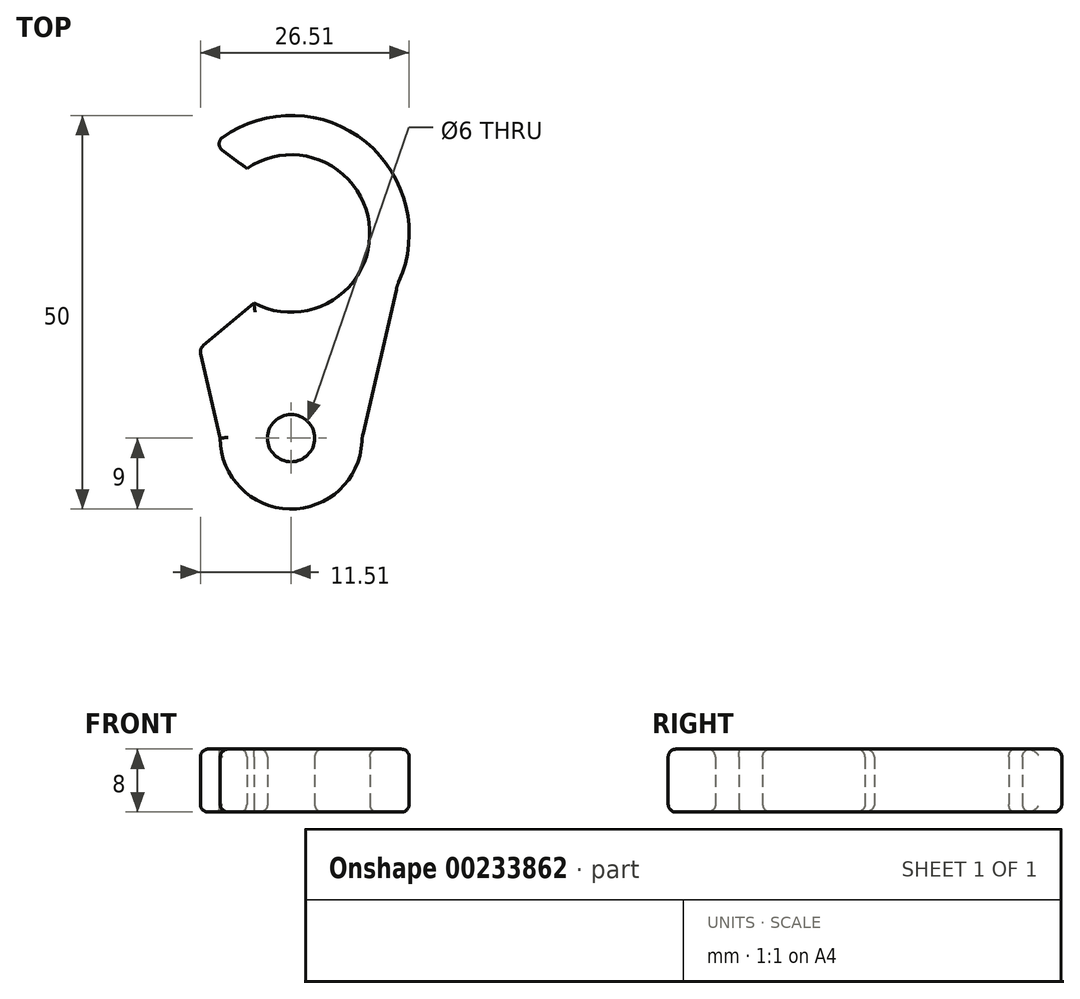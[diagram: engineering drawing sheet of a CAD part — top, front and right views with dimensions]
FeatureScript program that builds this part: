
annotation { "Feature Type Name" : "Feature", "Feature Type Description" : "" }
export const myFeature = defineFeature(function(context is Context, id is Id, definition is map)
    precondition{}
    {
        {
            var Q0;
            Q0=qCreatedBy(makeId("Top.planeOp"),FACE);
            var sketch = newSketch(context, id + "F0", { "sketchPlane" : qUnion([Q0])});
            skCircle(sketch, "E0", {"center": v(0, 0) * mm, "radius": 10 * mm});
            skCircle(sketch, "E1", {"center": v(0, 0) * mm, "radius": 15 * mm});
            skLineSegment(sketch, "E2", {"start": v(0, 0) * mm, "end": v(0, -26) * mm});
            skCircle(sketch, "E3", {"center": v(0, -26) * mm, "radius": 3 * mm});
            skCircle(sketch, "E4", {"center": v(0, -26) * mm, "radius": 9 * mm});
            skLineSegment(sketch, "E5", {"start": v(0, 0) * mm, "end": v(-15, 0) * mm});
            skLineSegment(sketch, "E6", {"start": v(-15, 0) * mm, "end": v(-9, -26) * mm});
            skLineSegment(sketch, "E7", {"start": v(0, 0) * mm, "end": v(15, 0) * mm});
            skLineSegment(sketch, "E8", {"start": v(15, 0) * mm, "end": v(9, -26) * mm});
            skLineSegment(sketch, "E9", {"start": v(-9.8, 11.36) * mm, "end": v(-5.61, 8.28) * mm});
            skLineSegment(sketch, "E10", {"start": v(-4.72, -8.81) * mm, "end": v(-11.62, -14.65) * mm});
            skSolve(sketch);
        }
        {
            var Q0;
            {var subQ0=sQuery(id+"F0.wireOp",EDGE,"E9");Q0=makeQuery(id+"F0.imprint","IMPRINT",FACE,{"disambiguationData":[TD([[makeQuery(id+"F0.imprint","IMPRINT",EDGE,{"derivedFrom":subQ0}),1.0]])]});}
            var Q1;
            {var subQ1=sQuery(id+"F0.wireOp",EDGE,"E0");var subQ6=sQuery(id+"F0.wireOp",EDGE,"E7");var subQ8=makeQuery(id+"F0.imprint","INTERSECT",VERTEX,{"derivedFrom":[subQ1,subQ6]});Q1=makeQuery(id+"F0.imprint","IMPRINT",FACE,{"disambiguationData":[TD([[makeQuery(id+"F0.imprint","IMPRINT",EDGE,{"disambiguationData":[TD([[subQ8,1.0]])],"derivedFrom":subQ1}),-1.0]])]});}
            var Q2;
            {var subQ0=sQuery(id+"F0.wireOp",EDGE,"E8");var subQ1=sQuery(id+"F0.wireOp",EDGE,"E1");var subQ2=makeQuery(id+"F0.imprint","INTERSECT",VERTEX,{"derivedFrom":[subQ1,subQ0]});Q2=makeQuery(id+"F0.imprint","IMPRINT",FACE,{"disambiguationData":[TD([[makeQuery(id+"F0.imprint","IMPRINT",EDGE,{"disambiguationData":[TD([[subQ2,1.0]])],"derivedFrom":subQ1}),-1.0]])]});}
            var Q3;
            Q3=makeQuery(id+"F0.imprint","IMPRINT",FACE,{"disambiguationData":[TD([[makeQuery(id+"F0.imprint","IMPRINT",EDGE,{"derivedFrom":sQuery(id+"F0.wireOp",EDGE,"E3")}),-1.0]])]});
            var Q4;
            {var subQ3=sQuery(id+"F0.wireOp",EDGE,"E10");var subQ5=sQuery(id+"F0.wireOp",EDGE,"E1");var subQ6=makeQuery(id+"F0.imprint","INTERSECT",VERTEX,{"derivedFrom":[subQ5,subQ3]});Q4=makeQuery(id+"F0.imprint","IMPRINT",FACE,{"disambiguationData":[TD([[makeQuery(id+"F0.imprint","IMPRINT",EDGE,{"disambiguationData":[TD([[subQ6,-1.0]])],"derivedFrom":subQ5}),-1.0]])]});}
            var Q5;
            {var subQ0=sQuery(id+"F0.wireOp",EDGE,"E10");var subQ1=sQuery(id+"F0.wireOp",EDGE,"E0");var subQ2=makeQuery(id+"F0.imprint","INTERSECT",VERTEX,{"derivedFrom":[subQ1,subQ0]});Q5=makeQuery(id+"F0.imprint","IMPRINT",FACE,{"disambiguationData":[TD([[makeQuery(id+"F0.imprint","IMPRINT",EDGE,{"disambiguationData":[TD([[subQ2,-1.0]])],"derivedFrom":subQ1}),-1.0]])]});}
            var Q6;
            {var subQ0=sQuery(id+"F0.wireOp",EDGE,"E8");var subQ1=sQuery(id+"F0.wireOp",EDGE,"E1");var subQ3=makeQuery(id+"F0.imprint","INTERSECT",VERTEX,{"derivedFrom":[subQ1,subQ0]});Q6=makeQuery(id+"F0.imprint","IMPRINT",FACE,{"disambiguationData":[TD([[makeQuery(id+"F0.imprint","IMPRINT",EDGE,{"disambiguationData":[TD([[subQ3,-1.0]])],"derivedFrom":subQ1}),1.0]])]});}
            extrude(context, id + "F1", {"entities" : qUnion([Q0, Q1, Q2, Q3, Q4, Q5, Q6]), "depth" : 8 * mm});
        }
        {
            var Q0;
            Q0=makeQuery(id+"F1.opExtrude","SWEPT_EDGE",EDGE,{"disambiguationData":[OSD([sQuery(id+"F0.wireOp",EDGE,"E1"),sQuery(id+"F0.wireOp",EDGE,"E8")])]});
            var Q1;
            Q1=makeQuery(id+"F1.opExtrude","SWEPT_EDGE",EDGE,{"disambiguationData":[OSD([sQuery(id+"F0.wireOp",EDGE,"E4"),sQuery(id+"F0.wireOp",EDGE,"E8")])]});
            fillet(context, id + "F2", {"entities" : qUnion([Q0, Q1]), "radius" : 5 * mm, "tangentPropagation" : true, "allowEdgeOverflow" : false});
        }
        {
            var Q0;
            Q0=makeQuery(id+"F1.opExtrude","CAP_EDGE",EDGE,{"disambiguationData":[OSD([sQuery(id+"F0.wireOp",EDGE,"E3")])],"isStart":true});
            var Q1;
            Q1=makeQuery(id+"F1.opExtrude","CAP_EDGE",EDGE,{"disambiguationData":[OSD([sQuery(id+"F0.wireOp",EDGE,"E3")])],"isStart":false});
            var Q2;
            Q2=makeQuery(id+"F1.opExtrude","CAP_EDGE",EDGE,{"disambiguationData":[OSD([sQuery(id+"F0.wireOp",EDGE,"E0")])],"isStart":false});
            var Q3;
            Q3=makeQuery(id+"F1.opExtrude","CAP_EDGE",EDGE,{"disambiguationData":[OSD([sQuery(id+"F0.wireOp",EDGE,"E0")])],"isStart":true});
            var Q4;
            Q4=makeQuery(id+"F1.opExtrude","CAP_EDGE",EDGE,{"disambiguationData":[OSD([sQuery(id+"F0.wireOp",EDGE,"E10")])],"isStart":false});
            var Q5;
            Q5=makeQuery(id+"F1.opExtrude","CAP_EDGE",EDGE,{"disambiguationData":[OSD([sQuery(id+"F0.wireOp",EDGE,"E10")])],"isStart":true});
            var Q6;
            Q6=makeQuery(id+"F1.opExtrude","SWEPT_EDGE",EDGE,{"disambiguationData":[OSD([sQuery(id+"F0.wireOp",EDGE,"E6"),sQuery(id+"F0.wireOp",EDGE,"E10")])]});
            var Q7;
            Q7=makeQuery(id+"F1.opExtrude","CAP_EDGE",EDGE,{"disambiguationData":[OSD([sQuery(id+"F0.wireOp",EDGE,"E6")])],"isStart":false});
            var Q8;
            Q8=makeQuery(id+"F1.opExtrude","CAP_EDGE",EDGE,{"disambiguationData":[OSD([sQuery(id+"F0.wireOp",EDGE,"E6")])],"isStart":true});
            var Q9;
            Q9=makeQuery(id+"F1.opExtrude","SWEPT_EDGE",EDGE,{"disambiguationData":[OSD([sQuery(id+"F0.wireOp",EDGE,"E1"),sQuery(id+"F0.wireOp",EDGE,"E9")])]});
            var Q10;
            Q10=makeQuery(id+"F1.opExtrude","CAP_EDGE",EDGE,{"disambiguationData":[OSD([sQuery(id+"F0.wireOp",EDGE,"E1")])],"isStart":true});
            var Q11;
            Q11=makeQuery(id+"F1.opExtrude","CAP_EDGE",EDGE,{"disambiguationData":[OSD([sQuery(id+"F0.wireOp",EDGE,"E1")])],"isStart":false});
            fillet(context, id + "F3", {"entities" : qUnion([Q0, Q1, Q2, Q3, Q4, Q5, Q6, Q7, Q8, Q9, Q10, Q11]), "radius" : 1 * mm, "tangentPropagation" : true, "allowEdgeOverflow" : false});
        }
    });
